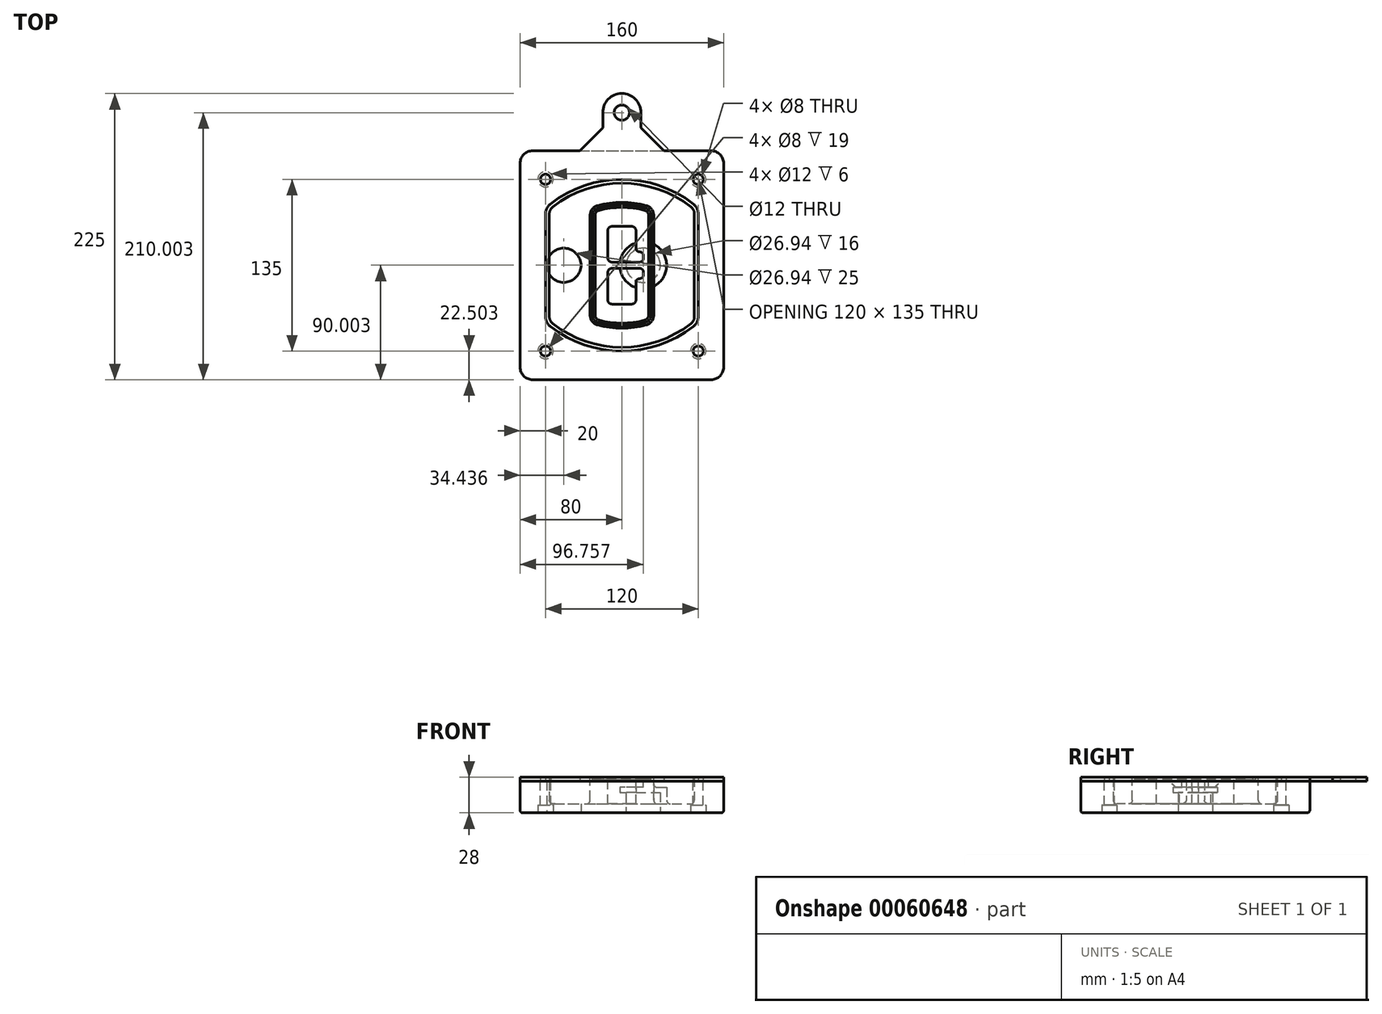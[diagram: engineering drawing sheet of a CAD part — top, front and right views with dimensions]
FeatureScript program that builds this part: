
annotation { "Feature Type Name" : "Feature", "Feature Type Description" : "" }
export const myFeature = defineFeature(function(context is Context, id is Id, definition is map)
    precondition{}
    {
        {
            var Q0;
            Q0=qCreatedBy(makeId("Top.planeOp"),FACE);
            var sketch = newSketch(context, id + "F0", { "sketchPlane" : qUnion([Q0])});
            skPoint(sketch, "E0.rect.middle", {"position": v(0, 0) * mm});
            skLineSegment(sketch, "E1.bottom", {"start": v(24.05, 28.38) * mm, "end": v(164.05, 28.38) * mm});
            skLineSegment(sketch, "E1.top", {"start": v(24.05, 208.38) * mm, "end": v(164.05, 208.38) * mm});
            skLineSegment(sketch, "E1.left", {"start": v(14.05, 38.38) * mm, "end": v(14.05, 198.38) * mm});
            skLineSegment(sketch, "E1.right", {"start": v(174.05, 38.38) * mm, "end": v(174.05, 198.38) * mm});
            skLineSegment(sketch, "E2", {"start": v(14.05, 208.38) * mm, "end": v(174.05, 28.38) * mm, "construction": true});
            skLineSegment(sketch, "E3", {"start": v(174.05, 208.38) * mm, "end": v(14.05, 28.38) * mm, "construction": true});
            skCircle(sketch, "E4", {"center": v(34.05, 185.88) * mm, "radius": 4 * mm});
            skCircle(sketch, "E5", {"center": v(154.05, 185.88) * mm, "radius": 4 * mm});
            skCircle(sketch, "E6", {"center": v(154.05, 50.88) * mm, "radius": 4 * mm});
            skCircle(sketch, "E7", {"center": v(34.05, 50.88) * mm, "radius": 4 * mm});
            skLineSegment(sketch, "E8", {"start": v(34.05, 185.88) * mm, "end": v(154.05, 185.88) * mm, "construction": true});
            skLineSegment(sketch, "E9", {"start": v(154.05, 185.88) * mm, "end": v(154.05, 50.88) * mm, "construction": true});
            skLineSegment(sketch, "E10", {"start": v(154.05, 50.88) * mm, "end": v(34.05, 50.88) * mm, "construction": true});
            skLineSegment(sketch, "E11", {"start": v(34.05, 50.88) * mm, "end": v(34.05, 185.88) * mm, "construction": true});
            skLineSegment(sketch, "E12", {"start": v(34.05, 158.68) * mm, "end": v(34.05, 78.09) * mm});
            skLineSegment(sketch, "E13", {"start": v(154.05, 158.68) * mm, "end": v(154.05, 78.09) * mm});
            skArc(sketch, "E14", {"start": v(150.2, 166.56) * mm, "mid": v(94.05, 185.88) * mm, "end": v(37.9, 166.56) * mm});
            skArc(sketch, "E15", {"start": v(37.9, 70.2) * mm, "mid": v(94.05, 50.88) * mm, "end": v(150.2, 70.2) * mm});
            skLineSegment(sketch, "E16", {"start": v(34.05, 118.38) * mm, "end": v(154.05, 118.38) * mm, "construction": true});
            skPoint(sketch, "E17.visualSharp", {"position": v(34.05, 73.38) * mm});
            skArc(sketch, "E17.filletArc", {"start": v(34.05, 78.09) * mm, "mid": v(35.06, 73.7) * mm, "end": v(37.9, 70.2) * mm});
            skPoint(sketch, "E18.visualSharp", {"position": v(34.05, 163.38) * mm});
            skArc(sketch, "E18.filletArc", {"start": v(37.9, 166.56) * mm, "mid": v(35.06, 163.06) * mm, "end": v(34.05, 158.68) * mm});
            skPoint(sketch, "E19.visualSharp", {"position": v(154.05, 163.38) * mm});
            skArc(sketch, "E19.filletArc", {"start": v(154.05, 158.68) * mm, "mid": v(153.04, 163.06) * mm, "end": v(150.2, 166.56) * mm});
            skPoint(sketch, "E20.visualSharp", {"position": v(154.05, 73.38) * mm});
            skArc(sketch, "E20.filletArc", {"start": v(150.2, 70.2) * mm, "mid": v(153.04, 73.7) * mm, "end": v(154.05, 78.09) * mm});
            skPoint(sketch, "E21.visualSharp", {"position": v(14.05, 208.38) * mm});
            skArc(sketch, "E21.filletArc", {"start": v(24.05, 208.38) * mm, "mid": v(16.98, 205.45) * mm, "end": v(14.05, 198.38) * mm});
            skPoint(sketch, "E22.visualSharp", {"position": v(174.05, 208.38) * mm});
            skArc(sketch, "E22.filletArc", {"start": v(174.05, 198.38) * mm, "mid": v(171.12, 205.45) * mm, "end": v(164.05, 208.38) * mm});
            skPoint(sketch, "E23.visualSharp", {"position": v(174.05, 28.38) * mm});
            skArc(sketch, "E23.filletArc", {"start": v(164.05, 28.38) * mm, "mid": v(171.12, 31.31) * mm, "end": v(174.05, 38.38) * mm});
            skPoint(sketch, "E24.visualSharp", {"position": v(14.05, 28.38) * mm});
            skArc(sketch, "E24.filletArc", {"start": v(14.05, 38.38) * mm, "mid": v(16.98, 31.31) * mm, "end": v(24.05, 28.38) * mm});
            skArc(sketch, "E25.0", {"start": v(151.05, 158.68) * mm, "mid": v(150.34, 161.75) * mm, "end": v(148.36, 164.2) * mm});
            skLineSegment(sketch, "E25.1", {"start": v(151.05, 158.68) * mm, "end": v(151.05, 78.09) * mm});
            skArc(sketch, "E25.2", {"start": v(148.36, 72.57) * mm, "mid": v(150.34, 75.02) * mm, "end": v(151.05, 78.09) * mm});
            skArc(sketch, "E25.3", {"start": v(39.74, 72.57) * mm, "mid": v(94.05, 53.88) * mm, "end": v(148.36, 72.57) * mm});
            skArc(sketch, "E25.4", {"start": v(37.05, 78.09) * mm, "mid": v(37.76, 75.02) * mm, "end": v(39.74, 72.57) * mm});
            skArc(sketch, "E25.5", {"start": v(148.36, 164.2) * mm, "mid": v(94.05, 182.88) * mm, "end": v(39.74, 164.2) * mm});
            skLineSegment(sketch, "E25.6", {"start": v(37.05, 158.68) * mm, "end": v(37.05, 78.09) * mm});
            skArc(sketch, "E25.7", {"start": v(39.74, 164.2) * mm, "mid": v(37.76, 161.75) * mm, "end": v(37.05, 158.68) * mm});
            skArc(sketch, "E26.0", {"start": v(35.43, 169.71) * mm, "mid": v(31.47, 164.82) * mm, "end": v(30.05, 158.68) * mm});
            skArc(sketch, "E26.1", {"start": v(152.67, 169.71) * mm, "mid": v(94.05, 189.88) * mm, "end": v(35.43, 169.71) * mm});
            skArc(sketch, "E26.2", {"start": v(158.05, 158.68) * mm, "mid": v(156.63, 164.82) * mm, "end": v(152.67, 169.71) * mm});
            skLineSegment(sketch, "E26.3", {"start": v(158.05, 158.68) * mm, "end": v(158.05, 78.09) * mm});
            skArc(sketch, "E26.4", {"start": v(152.67, 67.05) * mm, "mid": v(156.63, 71.95) * mm, "end": v(158.05, 78.09) * mm});
            skLineSegment(sketch, "E26.5", {"start": v(30.05, 158.68) * mm, "end": v(30.05, 78.09) * mm});
            skArc(sketch, "E26.6", {"start": v(35.43, 67.05) * mm, "mid": v(94.05, 46.88) * mm, "end": v(152.67, 67.05) * mm});
            skArc(sketch, "E26.7", {"start": v(30.05, 78.09) * mm, "mid": v(31.47, 71.95) * mm, "end": v(35.43, 67.05) * mm});
            skSolve(sketch);
        }
        {
            var Q0;
            Q0=makeQuery(id+"F0.imprint","IMPRINT",FACE,{"disambiguationData":[TD([[makeQuery(id+"F0.imprint","IMPRINT",EDGE,{"derivedFrom":sQuery(id+"F0.wireOp",EDGE,"E1.bottom")}),1.0]])]});
            var Q1;
            Q1=makeQuery(id+"F0.imprint","IMPRINT",FACE,{"disambiguationData":[TD([[makeQuery(id+"F0.imprint","IMPRINT",EDGE,{"derivedFrom":sQuery(id+"F0.wireOp",EDGE,"E12")}),1.0]])]});
            var Q2;
            Q2=makeQuery(id+"F0.imprint","IMPRINT",FACE,{"disambiguationData":[TD([[makeQuery(id+"F0.imprint","IMPRINT",EDGE,{"derivedFrom":sQuery(id+"F0.wireOp",EDGE,"E25.0")}),1.0]])]});
            var Q3;
            Q3=makeQuery(id+"F0.imprint","IMPRINT",FACE,{"disambiguationData":[TD([[makeQuery(id+"F0.imprint","IMPRINT",EDGE,{"derivedFrom":sQuery(id+"F0.wireOp",EDGE,"E12")}),-1.0]])]});
            extrude(context, id + "F1", {"entities" : qUnion([Q0, Q1, Q2, Q3]), "oppositeDirection" : true, "depth" : 25 * mm});
        }
        {
            var Q0;
            Q0=makeQuery(id+"F0.imprint","IMPRINT",FACE,{"disambiguationData":[TD([[makeQuery(id+"F0.imprint","IMPRINT",EDGE,{"derivedFrom":sQuery(id+"F0.wireOp",EDGE,"E12")}),1.0]])]});
            extrude(context, id + "F2", {"entities" : qUnion([Q0]), "operationType" : NewBodyOperationType.ADD, "depth" : 3 * mm});
        }
        {
            var Q0;
            Q0=makeQuery(id+"F0.imprint","IMPRINT",FACE,{"disambiguationData":[TD([[makeQuery(id+"F0.imprint","IMPRINT",EDGE,{"derivedFrom":sQuery(id+"F0.wireOp",EDGE,"E25.0")}),1.0]])]});
            extrude(context, id + "F3", {"entities" : qUnion([Q0]), "operationType" : NewBodyOperationType.REMOVE, "oppositeDirection" : true, "depth" : 18 * mm});
        }
        {
            var Q0;
            Q0=makeQuery(id+"F2.opExtrude","CAP_FACE",FACE,{"disambiguationData":[OSD([sQuery(id+"F0.wireOp",EDGE,"E12"),sQuery(id+"F0.wireOp",EDGE,"E13"),sQuery(id+"F0.wireOp",EDGE,"E14"),sQuery(id+"F0.wireOp",EDGE,"E15"),sQuery(id+"F0.wireOp",EDGE,"E17.filletArc"),sQuery(id+"F0.wireOp",EDGE,"E18.filletArc"),sQuery(id+"F0.wireOp",EDGE,"E19.filletArc"),sQuery(id+"F0.wireOp",EDGE,"E20.filletArc"),sQuery(id+"F0.wireOp",EDGE,"E25.0"),sQuery(id+"F0.wireOp",EDGE,"E25.1"),sQuery(id+"F0.wireOp",EDGE,"E25.2"),sQuery(id+"F0.wireOp",EDGE,"E25.3"),sQuery(id+"F0.wireOp",EDGE,"E25.4"),sQuery(id+"F0.wireOp",EDGE,"E25.5"),sQuery(id+"F0.wireOp",EDGE,"E25.6"),sQuery(id+"F0.wireOp",EDGE,"E25.7")])],"isStart":false});
            var sketch = newSketch(context, id + "F4", { "sketchPlane" : qUnion([Q0])});
            skArc(sketch, "E27.0", {"start": v(74.97, 71.41) * mm, "mid": v(94.05, 68.88) * mm, "end": v(113.13, 71.41) * mm});
            skArc(sketch, "E28.0", {"start": v(113.13, 165.35) * mm, "mid": v(94.05, 167.88) * mm, "end": v(74.97, 165.35) * mm});
            skLineSegment(sketch, "E29", {"start": v(69.05, 157.63) * mm, "end": v(69.05, 79.14) * mm});
            skLineSegment(sketch, "E30", {"start": v(119.05, 157.63) * mm, "end": v(119.05, 79.14) * mm});
            skLineSegment(sketch, "E31", {"start": v(69.05, 163.48) * mm, "end": v(119.05, 163.48) * mm, "construction": true});
            skLineSegment(sketch, "E32", {"start": v(69.05, 73.28) * mm, "end": v(119.05, 73.28) * mm, "construction": true});
            skPoint(sketch, "E33.visualSharp", {"position": v(69.05, 163.48) * mm});
            skArc(sketch, "E33.filletArc", {"start": v(74.97, 165.35) * mm, "mid": v(70.7, 162.5) * mm, "end": v(69.05, 157.63) * mm});
            skPoint(sketch, "E34.visualSharp", {"position": v(119.05, 163.48) * mm});
            skArc(sketch, "E34.filletArc", {"start": v(119.05, 157.63) * mm, "mid": v(117.4, 162.5) * mm, "end": v(113.13, 165.35) * mm});
            skPoint(sketch, "E35.visualSharp", {"position": v(119.05, 73.28) * mm});
            skArc(sketch, "E35.filletArc", {"start": v(113.13, 71.41) * mm, "mid": v(117.4, 74.27) * mm, "end": v(119.05, 79.14) * mm});
            skPoint(sketch, "E36.visualSharp", {"position": v(69.05, 73.28) * mm});
            skArc(sketch, "E36.filletArc", {"start": v(69.05, 79.14) * mm, "mid": v(70.7, 74.27) * mm, "end": v(74.97, 71.41) * mm});
            skArc(sketch, "E37.0", {"start": v(148.36, 164.2) * mm, "mid": v(94.05, 182.88) * mm, "end": v(39.74, 164.2) * mm});
            skArc(sketch, "E37.1", {"start": v(39.74, 164.2) * mm, "mid": v(37.76, 161.75) * mm, "end": v(37.05, 158.68) * mm});
            skLineSegment(sketch, "E37.2", {"start": v(37.05, 158.68) * mm, "end": v(37.05, 78.09) * mm});
            skArc(sketch, "E37.3", {"start": v(37.05, 78.09) * mm, "mid": v(37.76, 75.02) * mm, "end": v(39.74, 72.57) * mm});
            skArc(sketch, "E37.4", {"start": v(39.74, 72.57) * mm, "mid": v(94.05, 53.88) * mm, "end": v(148.36, 72.57) * mm});
            skArc(sketch, "E37.5", {"start": v(148.36, 72.57) * mm, "mid": v(150.34, 75.02) * mm, "end": v(151.05, 78.09) * mm});
            skLineSegment(sketch, "E37.6", {"start": v(151.05, 158.68) * mm, "end": v(151.05, 78.09) * mm});
            skArc(sketch, "E37.7", {"start": v(151.05, 158.68) * mm, "mid": v(150.34, 161.75) * mm, "end": v(148.36, 164.2) * mm});
            skLineSegment(sketch, "E38.0", {"start": v(117.05, 157.63) * mm, "end": v(117.05, 79.14) * mm});
            skArc(sketch, "E38.1", {"start": v(112.61, 73.34) * mm, "mid": v(115.81, 75.49) * mm, "end": v(117.05, 79.14) * mm});
            skArc(sketch, "E38.2", {"start": v(75.49, 73.34) * mm, "mid": v(94.05, 70.88) * mm, "end": v(112.61, 73.34) * mm});
            skArc(sketch, "E38.3", {"start": v(71.05, 79.14) * mm, "mid": v(72.29, 75.49) * mm, "end": v(75.49, 73.34) * mm});
            skLineSegment(sketch, "E38.4", {"start": v(71.05, 157.63) * mm, "end": v(71.05, 79.14) * mm});
            skArc(sketch, "E38.5", {"start": v(117.05, 157.63) * mm, "mid": v(115.81, 161.28) * mm, "end": v(112.61, 163.42) * mm});
            skArc(sketch, "E38.6", {"start": v(75.49, 163.42) * mm, "mid": v(72.29, 161.28) * mm, "end": v(71.05, 157.63) * mm});
            skArc(sketch, "E38.7", {"start": v(112.61, 163.42) * mm, "mid": v(94.05, 165.88) * mm, "end": v(75.49, 163.42) * mm});
            skArc(sketch, "E39.0", {"start": v(115.05, 157.63) * mm, "mid": v(114.23, 160.06) * mm, "end": v(112.1, 161.5) * mm});
            skLineSegment(sketch, "E39.1", {"start": v(115.05, 157.63) * mm, "end": v(115.05, 79.14) * mm});
            skArc(sketch, "E39.2", {"start": v(112.1, 75.27) * mm, "mid": v(114.23, 76.7) * mm, "end": v(115.05, 79.14) * mm});
            skArc(sketch, "E39.3", {"start": v(76, 75.27) * mm, "mid": v(94.05, 72.88) * mm, "end": v(112.1, 75.27) * mm});
            skArc(sketch, "E39.4", {"start": v(73.05, 79.14) * mm, "mid": v(73.87, 76.7) * mm, "end": v(76, 75.27) * mm});
            skArc(sketch, "E39.5", {"start": v(112.1, 161.5) * mm, "mid": v(94.05, 163.88) * mm, "end": v(76, 161.5) * mm});
            skLineSegment(sketch, "E39.6", {"start": v(73.05, 157.63) * mm, "end": v(73.05, 79.14) * mm});
            skArc(sketch, "E39.7", {"start": v(76, 161.5) * mm, "mid": v(73.87, 160.06) * mm, "end": v(73.05, 157.63) * mm});
            skLineSegment(sketch, "E40", {"start": v(69.05, 118.38) * mm, "end": v(119.05, 118.38) * mm, "construction": true});
            skLineSegment(sketch, "E41", {"start": v(83.05, 123.88) * mm, "end": v(83.05, 145.88) * mm});
            skLineSegment(sketch, "E42", {"start": v(86.05, 148.88) * mm, "end": v(102.05, 148.88) * mm});
            skLineSegment(sketch, "E43", {"start": v(105.05, 145.88) * mm, "end": v(105.05, 131.88) * mm});
            skLineSegment(sketch, "E44", {"start": v(108.05, 128.88) * mm, "end": v(108.05, 128.88) * mm});
            skLineSegment(sketch, "E45", {"start": v(111.05, 125.88) * mm, "end": v(111.05, 123.88) * mm});
            skLineSegment(sketch, "E46", {"start": v(108.05, 120.88) * mm, "end": v(86.05, 120.88) * mm});
            skPoint(sketch, "E47.visualSharp", {"position": v(83.05, 148.88) * mm});
            skArc(sketch, "E47.filletArc", {"start": v(86.05, 148.88) * mm, "mid": v(83.93, 148) * mm, "end": v(83.05, 145.88) * mm});
            skPoint(sketch, "E48.visualSharp", {"position": v(105.05, 148.88) * mm});
            skArc(sketch, "E48.filletArc", {"start": v(105.05, 145.88) * mm, "mid": v(104.17, 148) * mm, "end": v(102.05, 148.88) * mm});
            skPoint(sketch, "E49.visualSharp", {"position": v(105.05, 128.88) * mm});
            skArc(sketch, "E49.filletArc", {"start": v(105.05, 131.88) * mm, "mid": v(105.93, 129.76) * mm, "end": v(108.05, 128.88) * mm});
            skPoint(sketch, "E50.visualSharp", {"position": v(111.05, 128.88) * mm});
            skArc(sketch, "E50.filletArc", {"start": v(111.05, 125.88) * mm, "mid": v(110.17, 128) * mm, "end": v(108.05, 128.88) * mm});
            skPoint(sketch, "E51.visualSharp", {"position": v(111.05, 120.88) * mm});
            skArc(sketch, "E51.filletArc", {"start": v(108.05, 120.88) * mm, "mid": v(110.17, 121.76) * mm, "end": v(111.05, 123.88) * mm});
            skPoint(sketch, "E52.visualSharp", {"position": v(83.05, 120.88) * mm});
            skArc(sketch, "E52.filletArc", {"start": v(83.05, 123.88) * mm, "mid": v(83.93, 121.76) * mm, "end": v(86.05, 120.88) * mm});
            skLineSegment(sketch, "E53.0.MirrorCS", {"start": v(108.05, 115.88) * mm, "end": v(86.05, 115.88) * mm});
            skArc(sketch, "E54.0.MirrorCS", {"start": v(83.05, 112.88) * mm, "mid": v(83.93, 115) * mm, "end": v(86.05, 115.88) * mm});
            skLineSegment(sketch, "E55.0.MirrorCS", {"start": v(83.05, 112.88) * mm, "end": v(83.05, 90.88) * mm});
            skArc(sketch, "E56.0.MirrorCS", {"start": v(86.05, 87.88) * mm, "mid": v(83.93, 88.76) * mm, "end": v(83.05, 90.88) * mm});
            skLineSegment(sketch, "E57.0.MirrorCS", {"start": v(86.05, 87.88) * mm, "end": v(102.05, 87.88) * mm});
            skArc(sketch, "E58.0.MirrorCS", {"start": v(105.05, 90.88) * mm, "mid": v(104.17, 88.76) * mm, "end": v(102.05, 87.88) * mm});
            skLineSegment(sketch, "E59.0.MirrorCS", {"start": v(105.05, 90.88) * mm, "end": v(105.05, 104.88) * mm});
            skArc(sketch, "E60.0.MirrorCS", {"start": v(105.05, 104.88) * mm, "mid": v(105.93, 107) * mm, "end": v(108.05, 107.88) * mm});
            skArc(sketch, "E61.0.MirrorCS", {"start": v(111.05, 110.88) * mm, "mid": v(110.17, 108.76) * mm, "end": v(108.05, 107.88) * mm});
            skLineSegment(sketch, "E62.0.MirrorCS", {"start": v(111.05, 110.88) * mm, "end": v(111.05, 112.88) * mm});
            skArc(sketch, "E63.0.MirrorCS", {"start": v(108.05, 115.88) * mm, "mid": v(110.17, 115) * mm, "end": v(111.05, 112.88) * mm});
            skSolve(sketch);
        }
        {
            var Q0;
            Q0=makeQuery(id+"F4.imprint","IMPRINT",FACE,{"disambiguationData":[TD([[makeQuery(id+"F4.imprint","IMPRINT",EDGE,{"derivedFrom":sQuery(id+"F4.wireOp",EDGE,"E27.0")}),1.0]])]});
            var Q1;
            Q1=makeQuery(id+"F4.imprint","IMPRINT",FACE,{"disambiguationData":[TD([[makeQuery(id+"F4.imprint","IMPRINT",EDGE,{"derivedFrom":sQuery(id+"F4.wireOp",EDGE,"E38.0")}),-1.0]])]});
            var Q2;
            Q2=makeQuery(id+"F4.imprint","IMPRINT",FACE,{"disambiguationData":[TD([[makeQuery(id+"F4.imprint","IMPRINT",EDGE,{"derivedFrom":sQuery(id+"F4.wireOp",EDGE,"E39.0")}),1.0]])]});
            extrude(context, id + "F5", {"entities" : qUnion([Q0, Q1, Q2]), "operationType" : NewBodyOperationType.ADD, "endBound" : BoundingType.UP_TO_NEXT, "oppositeDirection" : true, "depth" : 25 * mm});
        }
        {
            var Q0;
            Q0=makeQuery(id+"F4.imprint","IMPRINT",FACE,{"disambiguationData":[TD([[makeQuery(id+"F4.imprint","IMPRINT",EDGE,{"derivedFrom":sQuery(id+"F4.wireOp",EDGE,"E38.0")}),-1.0]])]});
            extrude(context, id + "F6", {"entities" : qUnion([Q0]), "operationType" : NewBodyOperationType.REMOVE, "oppositeDirection" : true, "depth" : 2 * mm});
        }
        {
            var Q0;
            Q0=makeQuery(id+"F1.opExtrude","CAP_FACE",FACE,{"disambiguationData":[OSD([sQuery(id+"F0.wireOp",EDGE,"E1.bottom"),sQuery(id+"F0.wireOp",EDGE,"E1.top"),sQuery(id+"F0.wireOp",EDGE,"E1.left"),sQuery(id+"F0.wireOp",EDGE,"E1.right"),sQuery(id+"F0.wireOp",EDGE,"E4"),sQuery(id+"F0.wireOp",EDGE,"E5"),sQuery(id+"F0.wireOp",EDGE,"E6"),sQuery(id+"F0.wireOp",EDGE,"E7"),sQuery(id+"F0.wireOp",EDGE,"E21.filletArc"),sQuery(id+"F0.wireOp",EDGE,"E22.filletArc"),sQuery(id+"F0.wireOp",EDGE,"E23.filletArc"),sQuery(id+"F0.wireOp",EDGE,"E24.filletArc")])],"isStart":false});
            var sketch = newSketch(context, id + "F7", { "sketchPlane" : qUnion([Q0])});
            skCircle(sketch, "E64", {"center": v(110.8, -118.38) * mm, "radius": 13.47 * mm});
            skCircle(sketch, "E65", {"center": v(48.49, -118.38) * mm, "radius": 13.47 * mm});
            skLineSegment(sketch, "E66", {"start": v(174.05, -118.38) * mm, "end": v(14.05, -118.38) * mm});
            skCircle(sketch, "E67", {"center": v(110.8, -118.38) * mm, "radius": 18.47 * mm});
            skCircle(sketch, "E68", {"center": v(154.05, -185.88) * mm, "radius": 6 * mm});
            skCircle(sketch, "E69", {"center": v(34.05, -185.88) * mm, "radius": 6 * mm});
            skCircle(sketch, "E70", {"center": v(34.05, -50.88) * mm, "radius": 6 * mm});
            skCircle(sketch, "E71", {"center": v(154.05, -50.88) * mm, "radius": 6 * mm});
            skSolve(sketch);
        }
        {
            var Q0;
            {var subQ1=sQuery(id+"F7.wireOp",EDGE,"E66");var subQ4=sQuery(id+"F7.wireOp",EDGE,"E64");var subQ6=makeQuery(id+"F7.imprint","INTERSECT",VERTEX,{"disambiguationData":[OD(0.0)],"derivedFrom":[subQ4,subQ1]});Q0=makeQuery(id+"F7.imprint","IMPRINT",FACE,{"disambiguationData":[TD([[makeQuery(id+"F7.imprint","IMPRINT",EDGE,{"disambiguationData":[TD([[subQ6,-1.0]])],"derivedFrom":subQ4}),-1.0]])]});}
            var Q1;
            {var subQ0=sQuery(id+"F7.wireOp",EDGE,"E66");var subQ1=sQuery(id+"F7.wireOp",EDGE,"E64");var subQ3=makeQuery(id+"F7.imprint","INTERSECT",VERTEX,{"disambiguationData":[OD(0.0)],"derivedFrom":[subQ1,subQ0]});Q1=makeQuery(id+"F7.imprint","IMPRINT",FACE,{"disambiguationData":[TD([[makeQuery(id+"F7.imprint","IMPRINT",EDGE,{"disambiguationData":[TD([[subQ3,-1.0]])],"derivedFrom":subQ1}),1.0]])]});}
            var Q2;
            {var subQ0=sQuery(id+"F7.wireOp",EDGE,"E66");var subQ1=sQuery(id+"F7.wireOp",EDGE,"E64");var subQ3=makeQuery(id+"F7.imprint","INTERSECT",VERTEX,{"disambiguationData":[OD(0.0)],"derivedFrom":[subQ1,subQ0]});Q2=makeQuery(id+"F7.imprint","IMPRINT",FACE,{"disambiguationData":[TD([[makeQuery(id+"F7.imprint","IMPRINT",EDGE,{"disambiguationData":[TD([[subQ3,1.0]])],"derivedFrom":subQ1}),1.0]])]});}
            var Q3;
            {var subQ1=sQuery(id+"F7.wireOp",EDGE,"E66");var subQ4=sQuery(id+"F7.wireOp",EDGE,"E64");var subQ6=makeQuery(id+"F7.imprint","INTERSECT",VERTEX,{"disambiguationData":[OD(0.0)],"derivedFrom":[subQ4,subQ1]});Q3=makeQuery(id+"F7.imprint","IMPRINT",FACE,{"disambiguationData":[TD([[makeQuery(id+"F7.imprint","IMPRINT",EDGE,{"disambiguationData":[TD([[subQ6,1.0]])],"derivedFrom":subQ4}),-1.0]])]});}
            extrude(context, id + "F8", {"entities" : qUnion([Q0, Q1, Q2, Q3]), "operationType" : NewBodyOperationType.ADD, "oppositeDirection" : true, "depth" : 20 * mm});
        }
        {
            var Q0;
            {var subQ0=sQuery(id+"F7.wireOp",EDGE,"E66");var subQ1=sQuery(id+"F7.wireOp",EDGE,"E64");var subQ3=makeQuery(id+"F7.imprint","INTERSECT",VERTEX,{"disambiguationData":[OD(0.0)],"derivedFrom":[subQ1,subQ0]});Q0=makeQuery(id+"F7.imprint","IMPRINT",FACE,{"disambiguationData":[TD([[makeQuery(id+"F7.imprint","IMPRINT",EDGE,{"disambiguationData":[TD([[subQ3,-1.0]])],"derivedFrom":subQ1}),1.0]])]});}
            var Q1;
            {var subQ0=sQuery(id+"F7.wireOp",EDGE,"E66");var subQ1=sQuery(id+"F7.wireOp",EDGE,"E64");var subQ3=makeQuery(id+"F7.imprint","INTERSECT",VERTEX,{"disambiguationData":[OD(0.0)],"derivedFrom":[subQ1,subQ0]});Q1=makeQuery(id+"F7.imprint","IMPRINT",FACE,{"disambiguationData":[TD([[makeQuery(id+"F7.imprint","IMPRINT",EDGE,{"disambiguationData":[TD([[subQ3,1.0]])],"derivedFrom":subQ1}),1.0]])]});}
            extrude(context, id + "F9", {"entities" : qUnion([Q0, Q1]), "operationType" : NewBodyOperationType.REMOVE, "oppositeDirection" : true, "depth" : 16 * mm});
        }
        {
            var Q0;
            {var subQ0=sQuery(id+"F7.wireOp",EDGE,"E66");var subQ1=sQuery(id+"F7.wireOp",EDGE,"E65");var subQ3=makeQuery(id+"F7.imprint","INTERSECT",VERTEX,{"disambiguationData":[OD(0.0)],"derivedFrom":[subQ1,subQ0]});Q0=makeQuery(id+"F7.imprint","IMPRINT",FACE,{"disambiguationData":[TD([[makeQuery(id+"F7.imprint","IMPRINT",EDGE,{"disambiguationData":[TD([[subQ3,-1.0]])],"derivedFrom":subQ1}),1.0]])]});}
            var Q1;
            {var subQ0=sQuery(id+"F7.wireOp",EDGE,"E66");var subQ1=sQuery(id+"F7.wireOp",EDGE,"E65");var subQ3=makeQuery(id+"F7.imprint","INTERSECT",VERTEX,{"disambiguationData":[OD(0.0)],"derivedFrom":[subQ1,subQ0]});Q1=makeQuery(id+"F7.imprint","IMPRINT",FACE,{"disambiguationData":[TD([[makeQuery(id+"F7.imprint","IMPRINT",EDGE,{"disambiguationData":[TD([[subQ3,1.0]])],"derivedFrom":subQ1}),1.0]])]});}
            extrude(context, id + "F10", {"entities" : qUnion([Q0, Q1]), "operationType" : NewBodyOperationType.REMOVE, "oppositeDirection" : true, "depth" : 25 * mm});
        }
        {
            var Q0;
            Q0=makeQuery(id+"F7.imprint","IMPRINT",FACE,{"disambiguationData":[TD([[makeQuery(id+"F7.imprint","IMPRINT",EDGE,{"derivedFrom":sQuery(id+"F7.wireOp",EDGE,"E68")}),1.0]])]});
            var Q1;
            Q1=makeQuery(id+"F7.imprint","IMPRINT",FACE,{"disambiguationData":[TD([[makeQuery(id+"F7.imprint","IMPRINT",EDGE,{"derivedFrom":makeQuery(id+"F1.opExtrude","CAP_EDGE",EDGE,{"disambiguationData":[OSD([sQuery(id+"F0.wireOp",EDGE,"E5")])],"isStart":false})}),-1.0]])]});
            var Q2;
            Q2=makeQuery(id+"F7.imprint","IMPRINT",FACE,{"disambiguationData":[TD([[makeQuery(id+"F7.imprint","IMPRINT",EDGE,{"derivedFrom":sQuery(id+"F7.wireOp",EDGE,"E69")}),1.0]])]});
            var Q3;
            Q3=makeQuery(id+"F7.imprint","IMPRINT",FACE,{"disambiguationData":[TD([[makeQuery(id+"F7.imprint","IMPRINT",EDGE,{"derivedFrom":makeQuery(id+"F1.opExtrude","CAP_EDGE",EDGE,{"disambiguationData":[OSD([sQuery(id+"F0.wireOp",EDGE,"E4")])],"isStart":false})}),-1.0]])]});
            var Q4;
            Q4=makeQuery(id+"F7.imprint","IMPRINT",FACE,{"disambiguationData":[TD([[makeQuery(id+"F7.imprint","IMPRINT",EDGE,{"derivedFrom":sQuery(id+"F7.wireOp",EDGE,"E70")}),1.0]])]});
            var Q5;
            Q5=makeQuery(id+"F7.imprint","IMPRINT",FACE,{"disambiguationData":[TD([[makeQuery(id+"F7.imprint","IMPRINT",EDGE,{"derivedFrom":makeQuery(id+"F1.opExtrude","CAP_EDGE",EDGE,{"disambiguationData":[OSD([sQuery(id+"F0.wireOp",EDGE,"E7")])],"isStart":false})}),-1.0]])]});
            var Q6;
            Q6=makeQuery(id+"F7.imprint","IMPRINT",FACE,{"disambiguationData":[TD([[makeQuery(id+"F7.imprint","IMPRINT",EDGE,{"derivedFrom":sQuery(id+"F7.wireOp",EDGE,"E71")}),1.0]])]});
            var Q7;
            Q7=makeQuery(id+"F7.imprint","IMPRINT",FACE,{"disambiguationData":[TD([[makeQuery(id+"F7.imprint","IMPRINT",EDGE,{"derivedFrom":makeQuery(id+"F1.opExtrude","CAP_EDGE",EDGE,{"disambiguationData":[OSD([sQuery(id+"F0.wireOp",EDGE,"E6")])],"isStart":false})}),-1.0]])]});
            extrude(context, id + "F11", {"entities" : qUnion([Q0, Q1, Q2, Q3, Q4, Q5, Q6, Q7]), "operationType" : NewBodyOperationType.REMOVE, "oppositeDirection" : true, "depth" : 6 * mm});
        }
        {
            var Q0;
            Q0=makeQuery(id+"F9.boolean.opBoolean","COPY",FACE,{"derivedFrom":makeQuery(id+"F9.opExtrude","CAP_FACE",FACE,{"disambiguationData":[OSD([sQuery(id+"F7.wireOp",EDGE,"E64")])],"isStart":false})});
            var sketch = newSketch(context, id + "F12", { "sketchPlane" : qUnion([Q0])});
            skArc(sketch, "E72.0", {"start": v(105.05, -100.83) * mm, "mid": v(96.62, -106.56) * mm, "end": v(92.5, -115.88) * mm});
            skArc(sketch, "E72.1", {"start": v(92.5, -120.88) * mm, "mid": v(96.62, -130.2) * mm, "end": v(105.05, -135.93) * mm});
            skLineSegment(sketch, "E73", {"start": v(92.5, -120.88) * mm, "end": v(108.05, -120.88) * mm});
            skLineSegment(sketch, "E74.0", {"start": v(108.05, -115.88) * mm, "end": v(92.5, -115.88) * mm});
            skArc(sketch, "E74.1", {"start": v(108.05, -115.88) * mm, "mid": v(110.17, -115) * mm, "end": v(111.05, -112.88) * mm});
            skLineSegment(sketch, "E74.2", {"start": v(111.05, -110.88) * mm, "end": v(111.05, -112.88) * mm});
            skArc(sketch, "E74.3", {"start": v(111.05, -110.88) * mm, "mid": v(110.17, -108.76) * mm, "end": v(108.05, -107.88) * mm});
            skArc(sketch, "E74.4", {"start": v(105.05, -104.88) * mm, "mid": v(105.93, -107) * mm, "end": v(108.05, -107.88) * mm});
            skLineSegment(sketch, "E74.5", {"start": v(105.05, -100.83) * mm, "end": v(105.05, -104.88) * mm});
            skLineSegment(sketch, "E74.7", {"start": v(108.05, -120.88) * mm, "end": v(92.5, -120.88) * mm});
            skArc(sketch, "E74.8", {"start": v(108.05, -120.88) * mm, "mid": v(110.17, -121.76) * mm, "end": v(111.05, -123.88) * mm});
            skLineSegment(sketch, "E74.9", {"start": v(111.05, -125.88) * mm, "end": v(111.05, -123.88) * mm});
            skArc(sketch, "E74.10", {"start": v(111.05, -125.88) * mm, "mid": v(110.17, -128) * mm, "end": v(108.05, -128.88) * mm});
            skArc(sketch, "E74.11", {"start": v(105.05, -131.88) * mm, "mid": v(105.93, -129.76) * mm, "end": v(108.05, -128.88) * mm});
            skLineSegment(sketch, "E74.12", {"start": v(105.05, -135.93) * mm, "end": v(105.05, -131.88) * mm});
            skPoint(sketch, "E75.orphan", {"position": v(105.05, -145.88) * mm});
            skPoint(sketch, "E76.orphan", {"position": v(86.05, -120.88) * mm});
            skPoint(sketch, "E77.orphan", {"position": v(86.05, -115.88) * mm});
            skPoint(sketch, "E78.orphan", {"position": v(105.05, -90.88) * mm});
            skSolve(sketch);
        }
        {
            var Q0;
            {var subQ7=sQuery(id+"F12.wireOp",EDGE,"E72.0");var subQ14=sQuery(id+"F12.wireOp",EDGE,"E72.1");var subQ16=sQuery(id+"F12.wireOp",EDGE,"E74.1");var subQ18=sQuery(id+"F12.wireOp",EDGE,"E74.8");Q0=qUnion([makeQuery(id+"F12.imprint","IMPRINT",FACE,{"disambiguationData":[TD([[makeQuery(id+"F12.imprint","IMPRINT",EDGE,{"derivedFrom":subQ7}),1.0]])]}),makeQuery(id+"F12.imprint","IMPRINT",FACE,{"disambiguationData":[TD([[makeQuery(id+"F12.imprint","IMPRINT",EDGE,{"derivedFrom":subQ14}),1.0]])]}),makeQuery(id+"F12.imprint","IMPRINT",FACE,{"disambiguationData":[TD([[makeQuery(id+"F12.imprint","IMPRINT",EDGE,{"derivedFrom":subQ16}),1.0]])]}),makeQuery(id+"F12.imprint","IMPRINT",FACE,{"disambiguationData":[TD([[makeQuery(id+"F12.imprint","IMPRINT",EDGE,{"derivedFrom":subQ18}),-1.0]])]})]);}
            var Q1;
            Q1=makeQuery(id+"F5.boolean.opBoolean","SPLIT",FACE,{"disambiguationData":[TD([makeQuery(id+"F5.opExtrude","SWEPT_FACE",FACE,{"disambiguationData":[OSD([sQuery(id+"F4.wireOp",EDGE,"E41")])]})])],"derivedFrom":makeQuery(id+"F3.boolean.opBoolean","COPY",FACE,{"derivedFrom":makeQuery(id+"F3.opExtrude","CAP_FACE",FACE,{"disambiguationData":[OSD([sQuery(id+"F0.wireOp",EDGE,"E25.0"),sQuery(id+"F0.wireOp",EDGE,"E25.1"),sQuery(id+"F0.wireOp",EDGE,"E25.2"),sQuery(id+"F0.wireOp",EDGE,"E25.3"),sQuery(id+"F0.wireOp",EDGE,"E25.4"),sQuery(id+"F0.wireOp",EDGE,"E25.5"),sQuery(id+"F0.wireOp",EDGE,"E25.6"),sQuery(id+"F0.wireOp",EDGE,"E25.7")])],"isStart":false})})});
            extrude(context, id + "F13", {"entities" : qUnion([Q0]), "operationType" : NewBodyOperationType.REMOVE, "endBound" : BoundingType.UP_TO_SURFACE, "endBoundEntityFace" : qUnion([Q1]), "depth" : 25 * mm});
        }
        {
            var Q0;
            Q0=makeQuery(id+"F3.boolean.opBoolean","COPY",EDGE,{"derivedFrom":makeQuery(id+"F3.opExtrude","CAP_EDGE",EDGE,{"disambiguationData":[OSD([sQuery(id+"F0.wireOp",EDGE,"E25.6")])],"isStart":false})});
            var Q1;
            Q1=makeQuery(id+"F8.boolean.opBoolean","INTERSECT",EDGE,{"derivedFrom":[makeQuery(id+"F5.opExtrude","SWEPT_FACE",FACE,{"disambiguationData":[OSD([sQuery(id+"F4.wireOp",EDGE,"E30")])]}),makeQuery(id+"F8.opExtrude","CAP_FACE",FACE,{"disambiguationData":[OSD([sQuery(id+"F7.wireOp",EDGE,"E67")])],"isStart":false})]});
            var Q2;
            Q2=makeQuery(id+"F8.boolean.opBoolean","INTERSECT",EDGE,{"disambiguationData":[OD(1.0)],"derivedFrom":[makeQuery(id+"F5.opExtrude","SWEPT_FACE",FACE,{"disambiguationData":[OSD([sQuery(id+"F4.wireOp",EDGE,"E30")])]}),makeQuery(id+"F8.opExtrude","SWEPT_FACE",FACE,{"disambiguationData":[OSD([sQuery(id+"F7.wireOp",EDGE,"E67")])]})]});
            var Q3;
            {var subQ0=sQuery(id+"F4.wireOp",EDGE,"E30");Q3=makeQuery(id+"F8.boolean.opBoolean","SPLIT",EDGE,{"disambiguationData":[TD([makeQuery(id+"F5.opExtrude","SWEPT_FACE",FACE,{"disambiguationData":[OSD([sQuery(id+"F4.wireOp",EDGE,"E35.filletArc")])]})])],"derivedFrom":makeQuery(id+"F5.opExtrude","CAP_EDGE",EDGE,{"disambiguationData":[OSD([subQ0])],"isStart":false})});}
            var Q4;
            {var subQ0=sQuery(id+"F0.wireOp",EDGE,"E25.7");var subQ1=sQuery(id+"F0.wireOp",EDGE,"E25.1");var subQ2=sQuery(id+"F0.wireOp",EDGE,"E25.6");var subQ3=sQuery(id+"F0.wireOp",EDGE,"E25.5");var subQ4=sQuery(id+"F0.wireOp",EDGE,"E25.4");var subQ5=sQuery(id+"F0.wireOp",EDGE,"E25.0");var subQ6=sQuery(id+"F0.wireOp",EDGE,"E25.2");var subQ7=sQuery(id+"F0.wireOp",EDGE,"E25.3");Q4=makeQuery(id+"F8.boolean.opBoolean","INTERSECT",EDGE,{"derivedFrom":[makeQuery(id+"F5.boolean.opBoolean","SPLIT",FACE,{"disambiguationData":[TD([makeQuery(id+"F2.opExtrude","SWEPT_FACE",FACE,{"disambiguationData":[OSD([subQ5])]})])],"derivedFrom":makeQuery(id+"F3.boolean.opBoolean","COPY",FACE,{"derivedFrom":makeQuery(id+"F3.opExtrude","CAP_FACE",FACE,{"disambiguationData":[OSD([subQ5,subQ1,subQ6,subQ7,subQ4,subQ3,subQ2,subQ0])],"isStart":false})})}),makeQuery(id+"F8.opExtrude","SWEPT_FACE",FACE,{"disambiguationData":[OSD([sQuery(id+"F7.wireOp",EDGE,"E67")])]})]});}
            var Q5;
            Q5=makeQuery(id+"F8.boolean.opBoolean","INTERSECT",EDGE,{"disambiguationData":[OD(0.0)],"derivedFrom":[makeQuery(id+"F5.opExtrude","SWEPT_FACE",FACE,{"disambiguationData":[OSD([sQuery(id+"F4.wireOp",EDGE,"E30")])]}),makeQuery(id+"F8.opExtrude","SWEPT_FACE",FACE,{"disambiguationData":[OSD([sQuery(id+"F7.wireOp",EDGE,"E67")])]})]});
            fillet(context, id + "F14", {"entities" : qUnion([Q0, Q1, Q2, Q3, Q4, Q5]), "radius" : 3 * mm, "tangentPropagation" : true, "allowEdgeOverflow" : false});
        }
        {
            var Q0;
            Q0=makeQuery(id+"F1.opExtrude","CAP_EDGE",EDGE,{"disambiguationData":[OSD([sQuery(id+"F0.wireOp",EDGE,"E1.bottom")])],"isStart":false});
            fillet(context, id + "F15", {"entities" : qUnion([Q0]), "radius" : 2 * mm, "tangentPropagation" : true, "allowEdgeOverflow" : false});
        }
        {
            var Q0;
            {var subQ0=sQuery(id+"F0.wireOp",EDGE,"E22.filletArc");var subQ1=sQuery(id+"F0.wireOp",EDGE,"E7");var subQ2=sQuery(id+"F0.wireOp",EDGE,"E6");var subQ3=sQuery(id+"F0.wireOp",EDGE,"E5");var subQ4=sQuery(id+"F0.wireOp",EDGE,"E4");var subQ5=sQuery(id+"F0.wireOp",EDGE,"E1.bottom");var subQ6=sQuery(id+"F0.wireOp",EDGE,"E21.filletArc");var subQ7=sQuery(id+"F0.wireOp",EDGE,"E1.top");var subQ8=sQuery(id+"F0.wireOp",EDGE,"E1.left");var subQ9=sQuery(id+"F0.wireOp",EDGE,"E1.right");var subQ10=sQuery(id+"F0.wireOp",EDGE,"E23.filletArc");var subQ11=sQuery(id+"F0.wireOp",EDGE,"E24.filletArc");Q0=makeQuery(id+"F2.boolean.opBoolean","SPLIT",FACE,{"disambiguationData":[TD([makeQuery(id+"F1.opExtrude","SWEPT_FACE",FACE,{"disambiguationData":[OSD([subQ5])]})])],"derivedFrom":makeQuery(id+"F1.opExtrude","CAP_FACE",FACE,{"disambiguationData":[OSD([subQ5,subQ7,subQ8,subQ9,subQ4,subQ3,subQ2,subQ1,subQ6,subQ0,subQ10,subQ11])],"isStart":true})});}
            var sketch = newSketch(context, id + "F16", { "sketchPlane" : qUnion([Q0])});
            skLineSegment(sketch, "E79", {"start": v(94.05, 208.38) * mm, "end": v(94.05, 238.38) * mm, "construction": true});
            skCircle(sketch, "E80", {"center": v(94.05, 238.38) * mm, "radius": 6 * mm});
            skLineSegment(sketch, "E81", {"start": v(61.05, 208.38) * mm, "end": v(79.05, 226.38) * mm});
            skLineSegment(sketch, "E82", {"start": v(79.05, 226.38) * mm, "end": v(79.05, 238.38) * mm});
            skArc(sketch, "E83", {"start": v(109.05, 238.38) * mm, "mid": v(94.05, 253.38) * mm, "end": v(79.05, 238.38) * mm});
            skLineSegment(sketch, "E84", {"start": v(109.05, 238.38) * mm, "end": v(109.05, 226.38) * mm});
            skLineSegment(sketch, "E85", {"start": v(109.05, 226.38) * mm, "end": v(127.05, 208.38) * mm});
            skLineSegment(sketch, "E86", {"start": v(14.05, 118.38) * mm, "end": v(174.05, 118.38) * mm, "construction": true});
            skLineSegment(sketch, "E87.MirrorCS", {"start": v(127.05, 208.38) * mm, "end": v(109.05, 226.38) * mm});
            skArc(sketch, "E88.MirrorCS", {"start": v(79.05, 238.38) * mm, "mid": v(94.05, 253.38) * mm, "end": v(109.05, 238.38) * mm});
            skLineSegment(sketch, "E89.MirrorCS", {"start": v(79.05, 226.38) * mm, "end": v(61.05, 208.38) * mm});
            skLineSegment(sketch, "E90.MirrorCS", {"start": v(79.05, 238.38) * mm, "end": v(79.05, 226.38) * mm});
            skLineSegment(sketch, "E91.MirrorCS", {"start": v(109.05, 226.38) * mm, "end": v(109.05, 238.38) * mm});
            skLineSegment(sketch, "E92.MirrorCS", {"start": v(174.05, 118.38) * mm, "end": v(14.05, 118.38) * mm, "construction": true});
            skLineSegment(sketch, "E93.MirrorCS", {"start": v(79.05, -1.62) * mm, "end": v(79.05, 10.38) * mm});
            skArc(sketch, "E94.MirrorCS", {"start": v(79.05, -1.62) * mm, "mid": v(94.05, -16.62) * mm, "end": v(109.05, -1.62) * mm});
            skLineSegment(sketch, "E95.MirrorCS", {"start": v(127.05, 28.38) * mm, "end": v(109.05, 10.38) * mm});
            skLineSegment(sketch, "E96.MirrorCS", {"start": v(79.05, 10.38) * mm, "end": v(61.05, 28.38) * mm});
            skCircle(sketch, "E97.MirrorC", {"center": v(94.05, -1.62) * mm, "radius": 6 * mm});
            skLineSegment(sketch, "E98.MirrorCS", {"start": v(109.05, 10.38) * mm, "end": v(109.05, -1.62) * mm});
            skLineSegment(sketch, "E99.MirrorCS", {"start": v(109.05, 10.38) * mm, "end": v(127.05, 28.38) * mm});
            skLineSegment(sketch, "E100.MirrorCS", {"start": v(61.05, 28.38) * mm, "end": v(79.05, 10.38) * mm});
            skLineSegment(sketch, "E101.MirrorCS", {"start": v(79.05, 10.38) * mm, "end": v(79.05, -1.62) * mm});
            skArc(sketch, "E102.MirrorCS", {"start": v(109.05, -1.62) * mm, "mid": v(94.05, -16.62) * mm, "end": v(79.05, -1.62) * mm});
            skLineSegment(sketch, "E103.MirrorCS", {"start": v(109.05, -1.62) * mm, "end": v(109.05, 10.38) * mm});
            skLineSegment(sketch, "E104.MirrorCS", {"start": v(94.05, 28.38) * mm, "end": v(94.05, -1.62) * mm, "construction": true});
            skSolve(sketch);
        }
        {
            var Q0;
            Q0=makeQuery(id+"F16.imprint","IMPRINT",FACE,{"disambiguationData":[TD([[makeQuery(id+"F16.imprint","IMPRINT",EDGE,{"derivedFrom":sQuery(id+"F16.wireOp",EDGE,"E80")}),-1.0]])]});
            var Q1;
            Q1=makeQuery(id+"F16.imprint","IMPRINT",FACE,{"disambiguationData":[TD([[makeQuery(id+"F16.imprint","IMPRINT",EDGE,{"derivedFrom":makeQuery(id+"F1.opExtrude","CAP_EDGE",EDGE,{"disambiguationData":[OSD([sQuery(id+"F0.wireOp",EDGE,"E1.left")])],"isStart":true})}),-1.0]])]});
            var Q2;
            Q2=makeQuery(id+"F16.imprint","IMPRINT",FACE,{"disambiguationData":[TD([[makeQuery(id+"F16.imprint","IMPRINT",EDGE,{"derivedFrom":sQuery(id+"F16.wireOp",EDGE,"E102.MirrorCS")}),-1.0]])]});
            var Q3;
            Q3=makeQuery(id+"F2.opExtrude","CAP_FACE",FACE,{"disambiguationData":[OSD([sQuery(id+"F0.wireOp",EDGE,"E12"),sQuery(id+"F0.wireOp",EDGE,"E13"),sQuery(id+"F0.wireOp",EDGE,"E14"),sQuery(id+"F0.wireOp",EDGE,"E15"),sQuery(id+"F0.wireOp",EDGE,"E17.filletArc"),sQuery(id+"F0.wireOp",EDGE,"E18.filletArc"),sQuery(id+"F0.wireOp",EDGE,"E19.filletArc"),sQuery(id+"F0.wireOp",EDGE,"E20.filletArc"),sQuery(id+"F0.wireOp",EDGE,"E25.0"),sQuery(id+"F0.wireOp",EDGE,"E25.1"),sQuery(id+"F0.wireOp",EDGE,"E25.2"),sQuery(id+"F0.wireOp",EDGE,"E25.3"),sQuery(id+"F0.wireOp",EDGE,"E25.4"),sQuery(id+"F0.wireOp",EDGE,"E25.5"),sQuery(id+"F0.wireOp",EDGE,"E25.6"),sQuery(id+"F0.wireOp",EDGE,"E25.7")])],"isStart":false});
            extrude(context, id + "F17", {"entities" : qUnion([Q0, Q1, Q2]), "endBound" : BoundingType.UP_TO_SURFACE, "endBoundEntityFace" : qUnion([Q3]), "depth" : 25 * mm});
        }
    });
